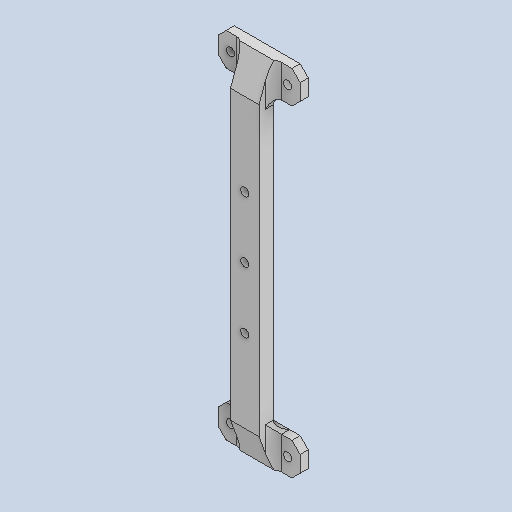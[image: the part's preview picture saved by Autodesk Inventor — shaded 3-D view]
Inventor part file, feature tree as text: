
AUTODESK INVENTOR PART (.ipt)
format: ipt  version: 2023 (Build 270158000, 158)  size: 196,608 bytes
history: native  units: mm
features: other x6, extrude x3, chamfer x3, sketch x3, projected_geometry x3, fillet x2, reference x2
ambient origin geometry x8: Origin, YZ Plane, XZ Plane, XY Plane, X Axis, Y Axis, Z Axis, Center Point
bodies: Solid1 (feature_tree)
feature tree (22):
  extrude  "Extrusion1"  Depth=2.0mm
  extrude  "Extrusion2"  Depth=2.0mm
  fillet  "Fillet1"  Radius=2.0mm
  fillet  "Fillet2"  Radius=7.0mm
  chamfer  "Chamfer1"  Distance=3.5mm
  chamfer  "Chamfer2"  Distance=2.0mm
  chamfer  "Chamfer3"  Distance=2.0mm
  extrude  "Extrusion3"  Depth=2.0mm TaperAngle=45.0deg
  sketch  "Sketch1"  dims[d0=2.0mm d1=2.0mm]
  reference  "Reference1"
  reference  "Reference2"
  sketch  "Sketch2"  dims[d2=2.0mm d3=2.0mm d4=2.0mm d5=0.0mm d6=7.0mm]
  projected_geometry  "Projected Loop1"
  projected_geometry  "Projected Loop2"
  sketch  "Sketch3"  dims[d7=87.0mm d8=3.5mm d9=0.0mm d10=2.0mm d11=2.0mm d12=2.0mm d13=2.0mm d14=45.0deg d15=3.0mm d16=2.0mm d17=12.217305mm d18=3.0mm d19=2.0mm d20=12.217305mm d21=2.0mm d22=15.0mm d23=2.0mm d24=15.0mm d25=2.0mm d26=3.5mm d27=0.0mm]
  projected_geometry  "Projected Loop3"
  parser-record x1  (decoder bookkeeping rows leaked as tree rows — omitted from the tree; the rows remain in map.json)
  other  "body_8d_1.iam"
  other  "leg_1_2d_MIR:1"
  other  "leg_holder_2_MIR:1"
  other  "leg_2d_1:1"
  other  "leg_holder_2:1"
note: 1 file-system path scrubbed to <path> (originals preserved in map.json)
